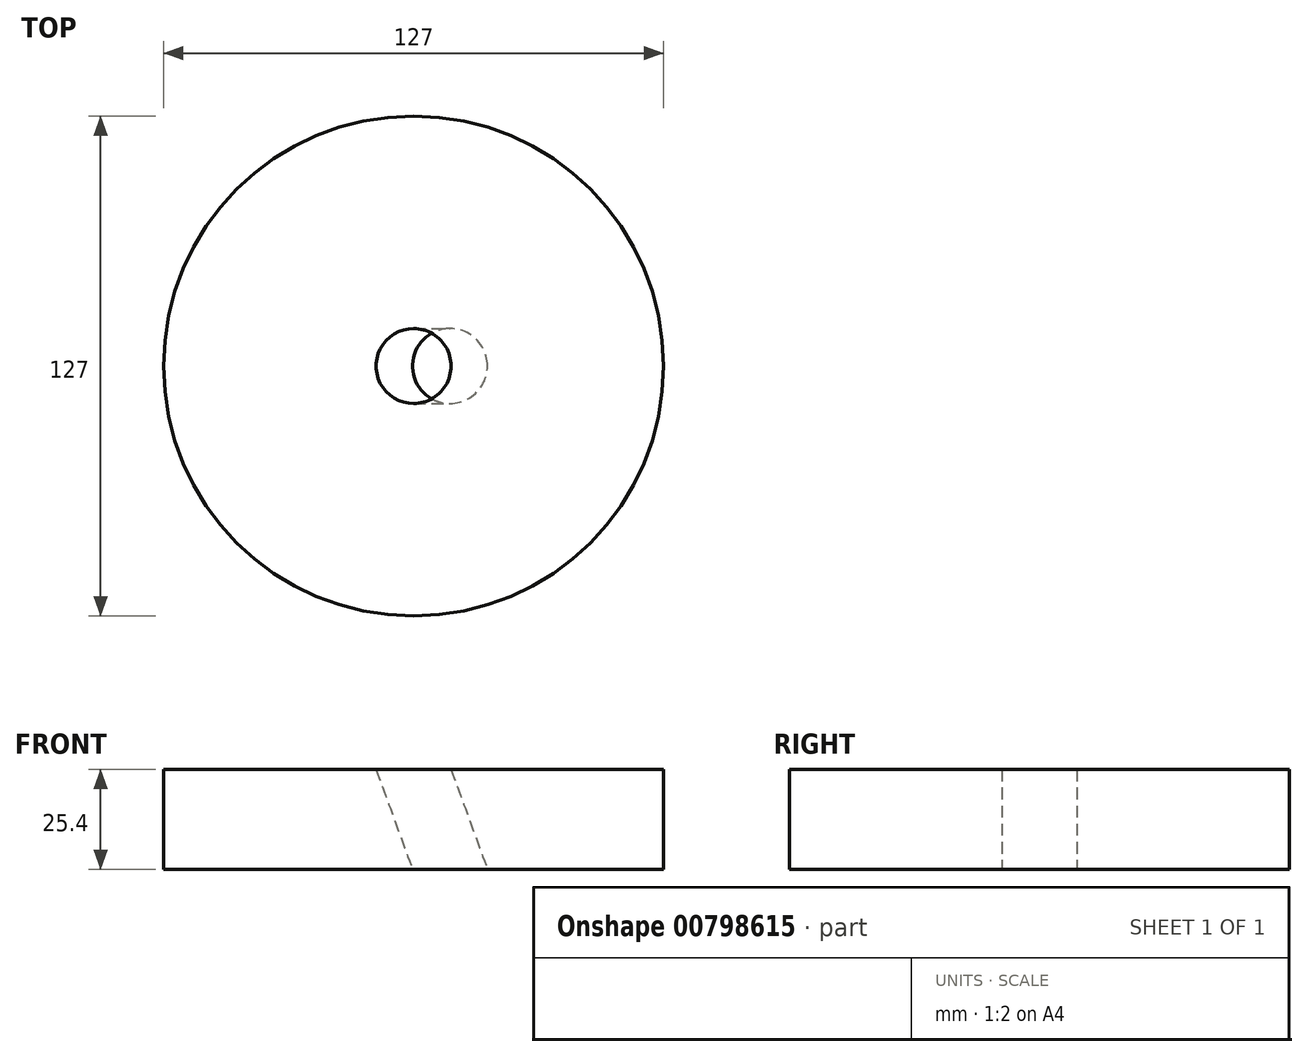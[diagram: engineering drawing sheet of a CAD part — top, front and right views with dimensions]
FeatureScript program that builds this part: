
annotation { "Feature Type Name" : "Feature", "Feature Type Description" : "" }
export const myFeature = defineFeature(function(context is Context, id is Id, definition is map)
    precondition{}
    {
        {
            var Q0;
            Q0=qCreatedBy(makeId("Top.planeOp"),FACE);
            var sketch = newSketch(context, id + "F0", { "sketchPlane" : qUnion([Q0])});
            skCircle(sketch, "E0", {"center": v(0, 0) * mm, "radius": 63.5 * mm});
            skSolve(sketch);
        }
        {
            var Q0;
            Q0=makeQuery(id+"F0.imprint","IMPRINT",FACE,{"disambiguationData":[TD([[makeQuery(id+"F0.imprint","IMPRINT",EDGE,{"derivedFrom":sQuery(id+"F0.wireOp",EDGE,"E0")}),1.0]])]});
            extrude(context, id + "F1", {"entities" : qUnion([Q0]), "depth" : 25.4 * mm, "offsetDistance" : 25.4 * mm});
        }
        {
            var Q0;
            Q0=makeQuery(id+"F1.opExtrude","CAP_FACE",FACE,{"disambiguationData":[OSD([sQuery(id+"F0.wireOp",EDGE,"E0")])],"isStart":false});
            var sketch = newSketch(context, id + "F2", { "sketchPlane" : qUnion([Q0])});
            skLineSegment(sketch, "E1", {"start": v(0, 0) * mm, "end": v(-46.4, 43.35) * mm});
            skLineSegment(sketch, "E2", {"start": v(-46.4, 43.35) * mm, "end": v(46.4, -43.35) * mm});
            skLineSegment(sketch, "E3", {"start": v(0, 0) * mm, "end": v(43.35, 46.4) * mm});
            skLineSegment(sketch, "E4", {"start": v(43.35, 46.4) * mm, "end": v(-43.35, -46.4) * mm});
            skCircle(sketch, "E5", {"center": v(0, 0) * mm, "radius": 9.53 * mm});
            skSolve(sketch);
        }
        {
            var Q0;
            Q0=qCreatedBy(makeId("Front.planeOp"),FACE);
            cPlane(context, id + "F3", {"entities" : qUnion([Q0]), "cplaneType" : CPlaneType.OFFSET, "offset" : 63.5 * mm, "width" : 152.4 * mm, "height" : 152.4 * mm});
        }
        {
            var Q0;
            Q0=qCreatedBy(id+"F3.planeOp",FACE);
            var sketch = newSketch(context, id + "F4", { "sketchPlane" : qUnion([Q0])});
            skLineSegment(sketch, "E6", {"start": v(0, 25.85) * mm, "end": v(0, 0) * mm});
            skLineSegment(sketch, "E7", {"start": v(0, 0) * mm, "end": v(9.4, 0) * mm});
            skLineSegment(sketch, "E8", {"start": v(9.4, 0) * mm, "end": v(0, 25.85) * mm});
            skSolve(sketch);
        }
        {
            var Q0;
            {var subQ0=sQuery(id+"F2.wireOp",EDGE,"E5");var subQ1=sQuery(id+"F2.wireOp",EDGE,"E2");var subQ2=makeQuery(id+"F2.imprint","INTERSECT",VERTEX,{"derivedFrom":[subQ1,subQ0]});Q0=makeQuery(id+"F2.imprint","IMPRINT",FACE,{"disambiguationData":[TD([[makeQuery(id+"F2.imprint","IMPRINT",EDGE,{"disambiguationData":[TD([[subQ2,-1.0]])],"derivedFrom":subQ0}),1.0]])]});}
            var Q1;
            {var subQ0=sQuery(id+"F2.wireOp",EDGE,"E5");var subQ1=sQuery(id+"F2.wireOp",EDGE,"E1");var subQ2=makeQuery(id+"F2.imprint","INTERSECT",VERTEX,{"derivedFrom":[subQ1,subQ0]});Q1=makeQuery(id+"F2.imprint","IMPRINT",FACE,{"disambiguationData":[TD([[makeQuery(id+"F2.imprint","IMPRINT",EDGE,{"disambiguationData":[TD([[subQ2,1.0]])],"derivedFrom":subQ0}),1.0]])]});}
            var Q2;
            {var subQ0=sQuery(id+"F2.wireOp",EDGE,"E5");var subQ1=sQuery(id+"F2.wireOp",EDGE,"E1");var subQ2=makeQuery(id+"F2.imprint","INTERSECT",VERTEX,{"derivedFrom":[subQ1,subQ0]});Q2=makeQuery(id+"F2.imprint","IMPRINT",FACE,{"disambiguationData":[TD([[makeQuery(id+"F2.imprint","IMPRINT",EDGE,{"disambiguationData":[TD([[subQ2,-1.0]])],"derivedFrom":subQ0}),1.0]])]});}
            var Q3;
            {var subQ0=sQuery(id+"F2.wireOp",EDGE,"E5");var subQ1=sQuery(id+"F2.wireOp",EDGE,"E2");var subQ2=makeQuery(id+"F2.imprint","INTERSECT",VERTEX,{"derivedFrom":[subQ1,subQ0]});Q3=makeQuery(id+"F2.imprint","IMPRINT",FACE,{"disambiguationData":[TD([[makeQuery(id+"F2.imprint","IMPRINT",EDGE,{"disambiguationData":[TD([[subQ2,1.0]])],"derivedFrom":subQ0}),1.0]])]});}
            var Q4;
            Q4=sQuery(id+"F4.wireOp",EDGE,"E8");
            sweep(context, id + "F5", {"operationType" : NewBodyOperationType.REMOVE, "profiles" : qUnion([Q0, Q1, Q2, Q3]), "path" : qUnion([Q4])});
        }
    });
